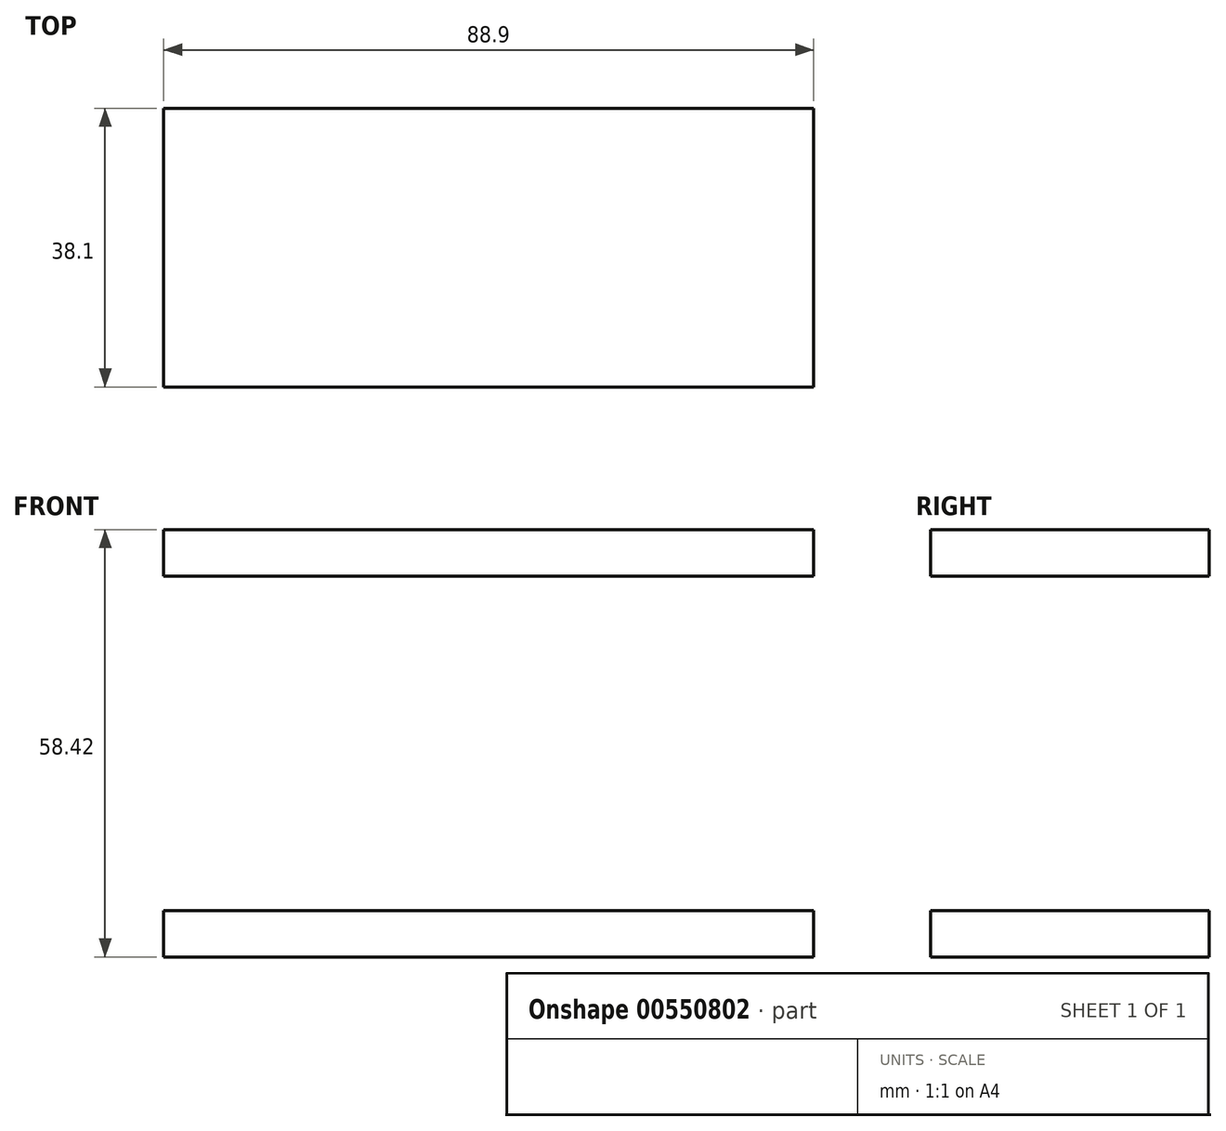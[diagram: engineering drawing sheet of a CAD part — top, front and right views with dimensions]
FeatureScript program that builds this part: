
annotation { "Feature Type Name" : "Feature", "Feature Type Description" : "" }
export const myFeature = defineFeature(function(context is Context, id is Id, definition is map)
    precondition{}
    {
        {
            var Q0;
            Q0=qCreatedBy(makeId("Front.planeOp"),FACE);
            var sketch = newSketch(context, id + "F0", { "sketchPlane" : qUnion([Q0])});
            skLineSegment(sketch, "E0.bottom", {"start": v(0, 0) * mm, "end": v(120.02, 0) * mm});
            skLineSegment(sketch, "E0.top", {"start": v(0, 152.4) * mm, "end": v(120.01, 152.4) * mm});
            skLineSegment(sketch, "E0.left", {"start": v(0, 0) * mm, "end": v(0, 152.4) * mm});
            skLineSegment(sketch, "E0.right", {"start": v(120.02, 0) * mm, "end": v(120.01, 152.4) * mm});
            skLineSegment(sketch, "E1.0", {"start": v(12.7, 139.7) * mm, "end": v(107.31, 139.7) * mm, "construction": true});
            skLineSegment(sketch, "E1.1", {"start": v(12.7, 12.7) * mm, "end": v(12.7, 139.7) * mm, "construction": true});
            skLineSegment(sketch, "E1.2", {"start": v(12.7, 12.7) * mm, "end": v(107.31, 12.7) * mm, "construction": true});
            skLineSegment(sketch, "E1.3", {"start": v(107.31, 12.7) * mm, "end": v(107.31, 139.7) * mm, "construction": true});
            skLineSegment(sketch, "E2.bottom", {"start": v(15.56, 121.92) * mm, "end": v(104.46, 121.92) * mm});
            skLineSegment(sketch, "E2.top", {"start": v(15.56, 115.57) * mm, "end": v(104.46, 115.57) * mm});
            skLineSegment(sketch, "E2.left", {"start": v(15.56, 121.92) * mm, "end": v(15.56, 115.57) * mm});
            skLineSegment(sketch, "E2.right", {"start": v(104.46, 121.92) * mm, "end": v(104.46, 115.57) * mm});
            skLineSegment(sketch, "E3.bottom", {"start": v(15.56, 69.85) * mm, "end": v(104.46, 69.85) * mm});
            skLineSegment(sketch, "E3.top", {"start": v(15.56, 63.5) * mm, "end": v(104.46, 63.5) * mm});
            skLineSegment(sketch, "E3.left", {"start": v(15.56, 69.85) * mm, "end": v(15.56, 63.5) * mm});
            skLineSegment(sketch, "E3.right", {"start": v(104.46, 69.85) * mm, "end": v(104.46, 63.5) * mm});
            skLineSegment(sketch, "E4", {"start": v(0, 50.8) * mm, "end": v(120.01, 50.8) * mm, "construction": true});
            skSolve(sketch);
        }
        {
            var Q0;
            Q0=makeQuery(id+"F0.imprint","IMPRINT",FACE,{"disambiguationData":[TD([[makeQuery(id+"F0.imprint","IMPRINT",EDGE,{"derivedFrom":sQuery(id+"F0.wireOp",EDGE,"E3.bottom")}),-1.0]])]});
            var Q1;
            Q1=makeQuery(id+"F0.imprint","IMPRINT",FACE,{"disambiguationData":[TD([[makeQuery(id+"F0.imprint","IMPRINT",EDGE,{"derivedFrom":sQuery(id+"F0.wireOp",EDGE,"E2.bottom")}),-1.0]])]});
            extrude(context, id + "F1", {"entities" : qUnion([Q0, Q1]), "depth" : 38.1 * mm, "offsetDistance" : 25.4 * mm});
        }
    });
